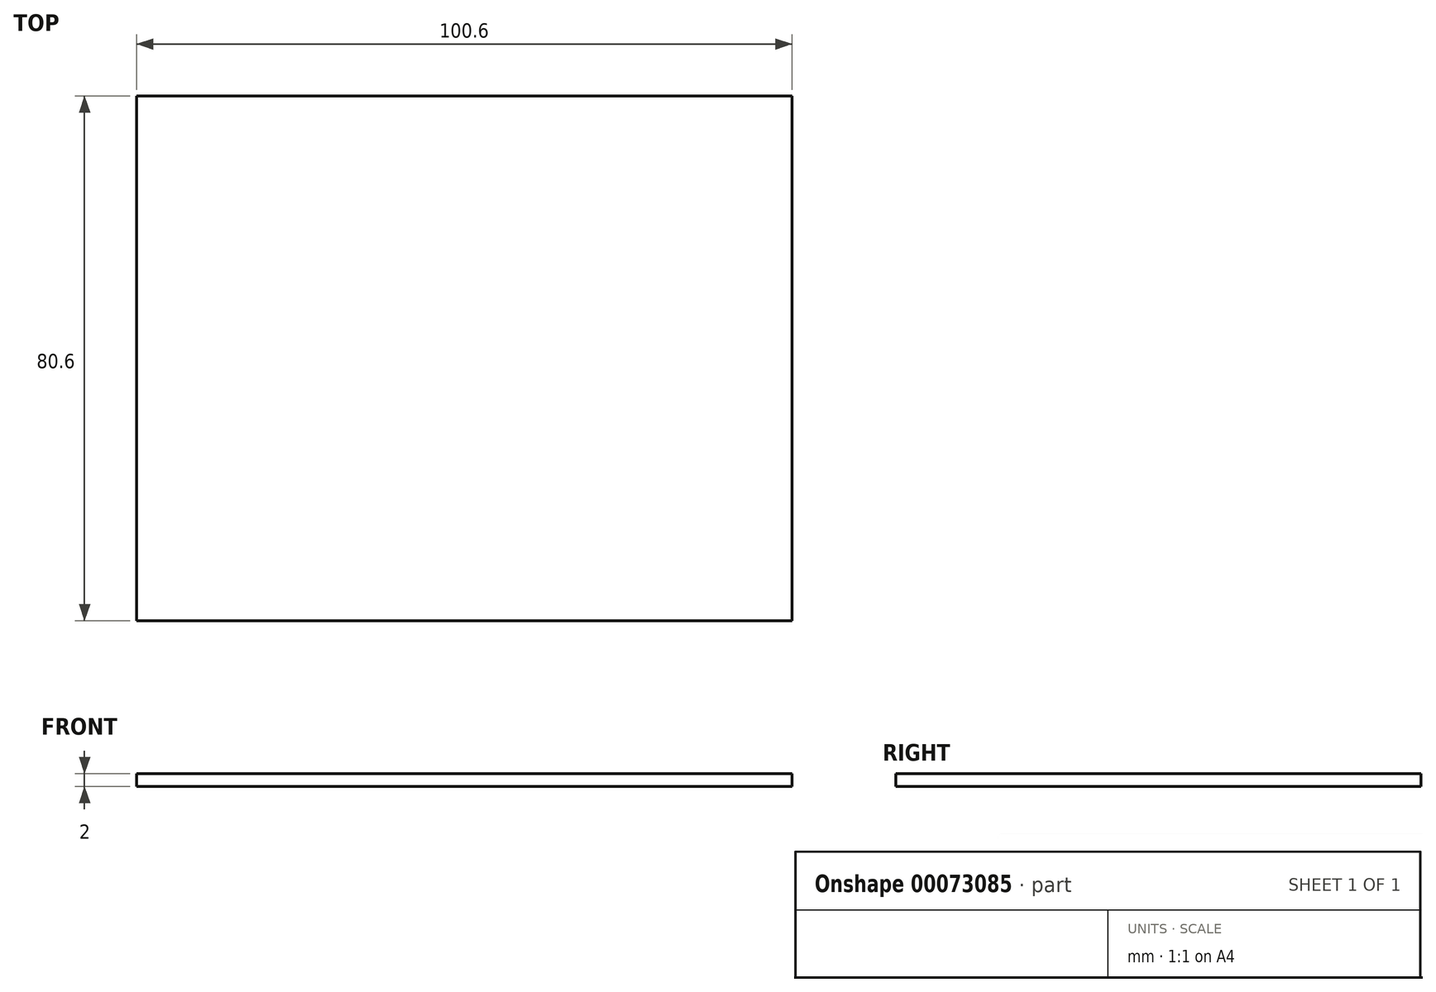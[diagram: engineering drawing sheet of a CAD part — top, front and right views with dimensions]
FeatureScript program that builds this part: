
annotation { "Feature Type Name" : "Feature", "Feature Type Description" : "" }
export const myFeature = defineFeature(function(context is Context, id is Id, definition is map)
    precondition{}
    {
        {
            var Q0;
            Q0=qCreatedBy(makeId("Top.planeOp"),FACE);
            var sketch = newSketch(context, id + "F0", { "sketchPlane" : qUnion([Q0])});
            skPoint(sketch, "E0.rect.middle", {"position": v(0, 0) * mm});
            skLineSegment(sketch, "E1.rect.bottom", {"start": v(-50.3, 40.3) * mm, "end": v(50.3, 40.3) * mm});
            skLineSegment(sketch, "E1.rect.left", {"start": v(-50.3, 40.3) * mm, "end": v(-50.3, -40.3) * mm});
            skLineSegment(sketch, "E1.rect.right", {"start": v(50.3, 40.3) * mm, "end": v(50.3, -40.3) * mm});
            skLineSegment(sketch, "E2", {"start": v(-50.3, -40.3) * mm, "end": v(50.3, -40.3) * mm});
            skSolve(sketch);
        }
        {
            var Q0;
            Q0=makeQuery(id+"F0.imprint","IMPRINT",FACE,{"disambiguationData":[TD([[makeQuery(id+"F0.imprint","IMPRINT",EDGE,{"derivedFrom":sQuery(id+"F0.wireOp",EDGE,"E1.rect.bottom")}),-1.0]])]});
            extrude(context, id + "F1", {"entities" : qUnion([Q0]), "depth" : 2 * mm});
        }
    });
